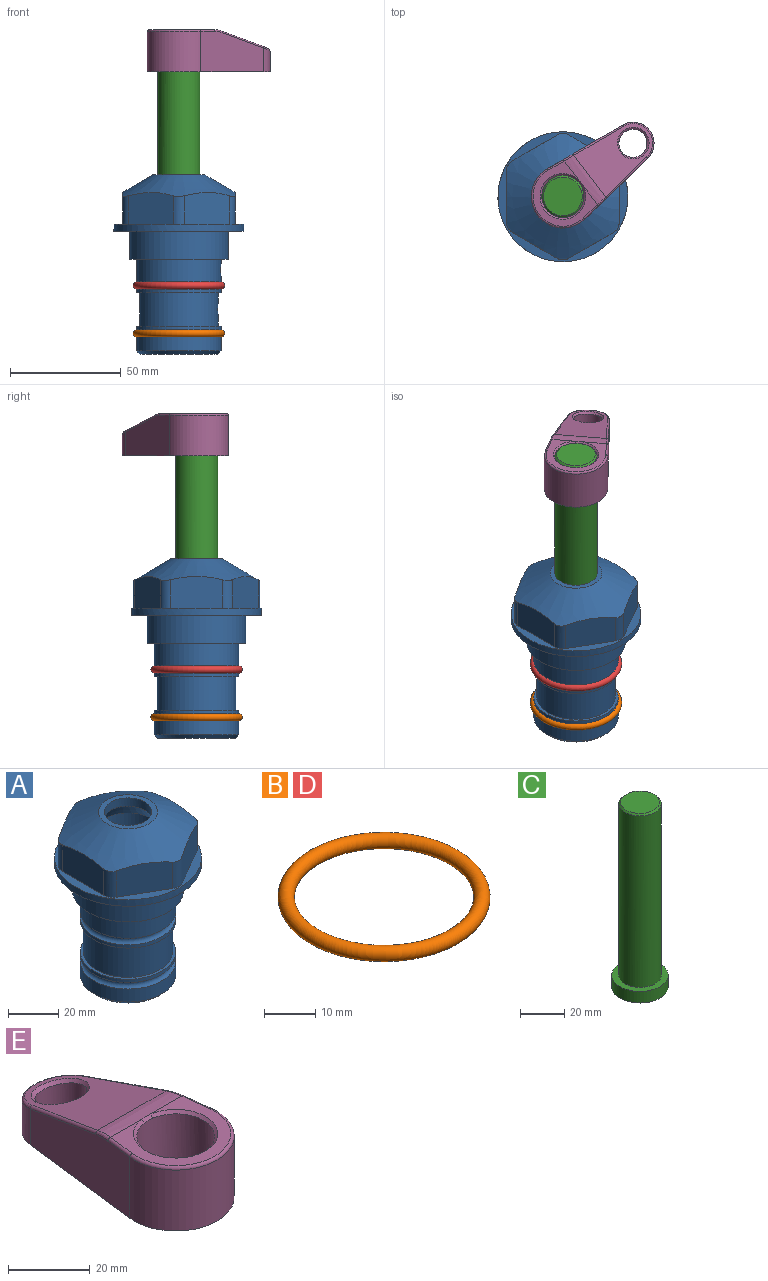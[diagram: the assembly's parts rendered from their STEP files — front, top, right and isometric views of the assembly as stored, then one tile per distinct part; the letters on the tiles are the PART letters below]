
ASSEMBLY  parts=5 mates=4
PART A: 36 faces, bbox 58.7x58.7x81 mm
  f0: cylinder r=17.78mm len=35.56mm, axis (0,0,1), area 1670.8mm2, adj f23,f24,f31
  f1: cylinder r=19.05mm len=38.1mm, axis (0,0,1), area 1191.9mm2, adj f26,f27,f30
  f2: plane 58.66x58.66mm, normal (0,0,-1), area 1150.6mm2, adj f3,f28
  f3: cylinder r=29.33mm len=58.66mm, axis (0,0,-1), area 585.1mm2, adj f2,f4
  f4: plane 58.66x58.66mm, normal (0,0,1), area 475.9mm2, adj f3,f5,f6,f7,f8,f9,f10,f11
  f5: plane 20.32x14.34mm, normal (-0.5,0.87,0), area 324.4mm2, adj f4,f15,f16,f17
  f6: plane 20.32x14.34mm, normal (0.5,0.87,0), area 324.4mm2, adj f4,f14,f15,f17
  f7: plane 23.48x14.34mm, normal (1,0,0), area 324.4mm2, adj f4,f13,f14,f17
  f8: plane 20.32x14.34mm, normal (0.5,-0.87,0), area 324.4mm2, adj f4,f12,f13,f17
  f9: plane 20.32x14.34mm, normal (-0.5,-0.87,0), area 324.4mm2, adj f4,f11,f12,f17
  f10: plane 23.48x14.34mm, normal (-1,0,0), area 324.4mm2, adj f4,f11,f16,f17
  f11: cylinder r=5.08mm len=12.85mm, axis (0,0,-1), area 67.2mm2, adj f4,f9,f10,f17
  f12: cylinder r=5.08mm len=12.85mm, axis (0,0,-1), area 67.2mm2, adj f4,f8,f9,f17
  f13: cylinder r=5.08mm len=12.85mm, axis (0,0,-1), area 67.2mm2, adj f4,f7,f8,f17
  f14: cylinder r=5.08mm len=12.85mm, axis (0,0,-1), area 67.2mm2, adj f4,f6,f7,f17
  f15: cylinder r=5.08mm len=12.85mm, axis (0,0,-1), area 67.2mm2, adj f4,f5,f6,f17
  f16: cylinder r=5.08mm len=12.85mm, axis (0,0,-1), area 67.2mm2, adj f4,f5,f10,f17
  f17: cone r=11.73mm half-angle=60deg, axis (0,0,-1), area 2071.8mm2, adj f5,f6,f7,f8,f9,f10,f11,f12
  f18: plane 23.46x23.46mm, normal (0,0,1), area 147.4mm2, adj f17,f35
  f19: plane 34.93x34.93mm, normal (0,0,-1), area 958mm2, adj f29
  f20: cylinder r=19.05mm len=38.1mm, axis (0,0,1), area 760.1mm2, adj f21,f29
  f21: torus R=19.05mm, axis (0,0,1), area 565.3mm2, adj f20,f22
  f22: cylinder r=19.05mm len=38.1mm, axis (0,0,1), area 190mm2, adj f21,f23
  f23: plane 38.1x38.1mm, normal (0,0,1), area 146.9mm2, adj f0,f22
  f24: plane 38.1x38.1mm, normal (0,0,-1), area 146.9mm2, adj f0,f25
  f25: cylinder r=19.05mm len=38.1mm, axis (0,0,1), area 190mm2, adj f24,f26
  f26: torus R=19.05mm, axis (0,0,1), area 565.3mm2, adj f1,f25
  f27: plane 44.45x44.45mm, normal (0,0,-1), area 411.7mm2, adj f1,f28
  f28: cylinder r=22.23mm len=44.45mm, axis (0,0,1), area 1773.5mm2, adj f2,f27
  f29: cone r=19.05mm half-angle=45deg, axis (0,0,1), area 257.5mm2, adj f19,f20
  f30: cylinder r=3.17mm len=6.75mm, axis (-1,0,0), area 128mm2, adj f1,f33
  f31: cylinder r=3.17mm len=6.35mm, axis (-1,0,0), area 102.5mm2, adj f0,f33
  f32: plane 25.4x25.4mm, normal (0,0,1), area 506.7mm2, adj f33
  f33: cylinder r=12.7mm len=66.42mm, axis (0,0,-1), area 5236.2mm2, adj f30,f31,f32,f34
  f34: cone r=9.53mm half-angle=30deg, axis (0,0,-1), area 443.4mm2, adj f33,f35
  f35: cylinder r=9.53mm len=19.05mm, axis (0,0,-1), area 240.9mm2, adj f18,f34
PART B: 1 faces, bbox 44.7x44.7x3.2 mm
  f0: torus R=19.05mm, axis (0,0,1), area 1193.9mm2
PART C: 6 faces, bbox 25.4x25.4x101.6 mm
  f0: plane 17.46x17.46mm, normal (0,0,1), area 239.5mm2, adj f5
  f1: plane 25.4x25.4mm, normal (0,0,-1), area 506.7mm2, adj f2
  f2: cylinder r=12.7mm len=25.4mm, axis (0,0,1), area 506.7mm2, adj f1,f3
  f3: plane 25.4x25.4mm, normal (0,0,1), area 221.7mm2, adj f2,f4
  f4: cylinder r=9.53mm len=94.46mm, axis (0,0,1), area 5653mm2, adj f3,f5
  f5: cone r=8.73mm half-angle=45deg, axis (0,0,-1), area 64.4mm2, adj f0,f4
PART D: same geometry as B
PART E: 31 faces, bbox 31.7x65.5x19.8 mm
  f0: plane 39.12x18.26mm, normal (0.99,0.12,0), area 612.2mm2, adj f1,f4,f7,f11,f13,f15
  f1: cylinder r=9.53mm len=18.91mm, axis (0,0,-1), area 296.1mm2, adj f0,f2,f7,f17
  f2: plane 39.12x18.26mm, normal (-0.99,0.12,0), area 612.2mm2, adj f1,f4,f7,f12,f14,f16
  f3: cylinder r=6.35mm len=12.7mm, axis (0,0,-1), area 362.4mm2, adj f7,f18
  f4: cylinder r=14.29mm len=28.58mm, axis (0,0,-1), area 882.2mm2, adj f0,f2,f7,f10
  f5: cylinder r=9.53mm len=19.05mm, axis (0,0,-1), area 1092.6mm2, adj f7,f19,f20
  f6: plane 26.99x23.69mm, normal (0,0,1), area 216.2mm2, adj f9,f10,f11,f12,f19
  f7: plane 63.5x28.58mm, normal (0,0,-1), area 661.8mm2, adj f0,f1,f2,f3,f4,f5,f22,f23
  f8: plane 33.52x23.6mm, normal (0,0.26,0.97), area 486mm2, adj f9,f15,f16,f17,f18
  f9: cylinder r=19.05mm len=24.72mm, axis (1,0,0), area 120.4mm2, adj f6,f8,f13,f14,f20
  f10: torus R=13.49mm, axis (0,0,1), area 59mm2, adj f4,f6,f11,f12
  f11: cylinder r=0.79mm len=8.67mm, axis (0.12,-0.99,0), area 10.8mm2, adj f0,f6,f10,f13
  f12: cylinder r=0.79mm len=8.67mm, axis (0.12,0.99,0), area 10.8mm2, adj f2,f6,f10,f14
  f13: bspline ~4.95x1.42mm, area 6.1mm2, adj f0,f9,f11,f15
  f14: bspline ~4.95x1.42mm, area 6.1mm2, adj f2,f9,f12,f16
  f15: cylinder r=0.79mm len=25.95mm, axis (0.12,-0.96,0.26), area 32.9mm2, adj f0,f8,f13,f17
  f16: cylinder r=0.79mm len=25.95mm, axis (0.12,0.96,-0.26), area 32.9mm2, adj f2,f8,f14,f17
  f17: bspline ~18.91x8.38mm, area 30mm2, adj f1,f8,f15,f16
  f18: bspline ~14.29x14.29mm, area 48.3mm2, adj f3,f8
  f19: cone r=9.53mm half-angle=45deg, axis (0,0,1), area 66.5mm2, adj f5,f6,f20
  f20: bspline ~3.22x0.96mm, area 3.5mm2, adj f5,f9,f19
  f21: plane 2.75x2.72mm, normal (0,0,-1), area 2.9mm2, adj f23,f25,f28
  f22: plane 23.05x15.88mm, normal (-0.99,-0.12,0), area 323.6mm2, adj f7,f25,f26,f27,f28,f29
  f23: plane 23.05x15.88mm, normal (0.99,-0.12,0), area 323.6mm2, adj f7,f21,f25,f27,f28,f30
  f24: cylinder r=9.53mm len=10.69mm, axis (0,0,-1), area 114.7mm2, adj f7,f27,f29,f30
  f25: cylinder r=12.7mm len=20.59mm, axis (0,0,-1), area 381.1mm2, adj f7,f21,f22,f23,f26,f28
  f26: plane 2.75x2.72mm, normal (0,0,-1), area 2.9mm2, adj f22,f25,f28
  f27: plane 19.72x18.37mm, normal (0,-0.26,-0.97), area 291.8mm2, adj f22,f23,f24,f28,f29,f30
  f28: cylinder r=15.88mm len=19.92mm, axis (1,0,0), area 54.8mm2, adj f21,f22,f23,f25,f26,f27
  f29: cylinder r=1.59mm len=11mm, axis (0,0,-1), area 34.7mm2, adj f7,f22,f24,f27
  f30: cylinder r=1.59mm len=11mm, axis (0,0,-1), area 34.7mm2, adj f7,f23,f24,f27
PLACE A at identity fixed
PLACE B t=(0,0,-21.59)mm
PLACE C rot(axis=(0,0,-1),52.9deg) t=(0,0,27.55)mm
PLACE D at identity
PLACE E rot(axis=(0,0,-1),52.9deg) t=(0,0,27.55)mm
MATE fastened D.f0 <-> A.f0  axis (0,0,1) through (0,0,-24.51)mm
MATE cylindrical A.f0 <-> C.f2  axis (0,0,1) through (0,0,-50.55)mm
MATE fastened C.f2 <-> E.f4  axis (0,0,1) through (0,0,91.05)mm
MATE fastened A.f0 <-> B.f0  axis (0,0,1) through (0,0,-46.1)mm
